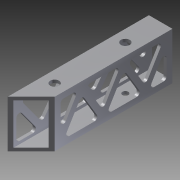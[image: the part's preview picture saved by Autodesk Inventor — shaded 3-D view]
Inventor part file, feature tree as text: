
AUTODESK INVENTOR PART (.ipt)
format: ipt  version: 2012 (Build 160160000, 160)  size: 280,064 bytes
history: native  units: in
note: dims shown in document units (in); Inventor stores cm internally (conversion verified against a paired STEP export)
features: extrude x6, sketch x5, fillet x1
ambient origin geometry x8: Origin, YZ Plane, XZ Plane, XY Plane, X Axis, Y Axis, Z Axis, Center Point
bodies: Solid1 (feature_tree)
feature tree (12):
  extrude  "Extrusion1"  Depth=1.0in
  sketch  "Sketch2"  dims[d2=0.125in d3=0.125in]
  extrude  "Extrusion2"  Depth=0.125in
  extrude  "Extrusion3"  Depth=0.125in
  extrude  "Extrusion4"  TaperAngle=45.0deg  [1 undecoded]
  extrude  "Extrusion5"  Depth=0.5in
  extrude  "Extrusion6"  Depth=1.5in
  fillet  "Fillet1"  Radius=3.0in
  sketch  "Sketch1"  dims[d0=2.0in d1=1.0in]
  sketch  "Sketch3"  dims[d4=0.125in d5=0.125in]
  sketch  "Sketch4"  dims[d6=6.0in d7=0.0in d8=45.0deg]
  sketch  "Sketch5"  dims[d9=0.25in d10=0.5in d11=1.5in d12=3.0in d13=0.125in d14=0.0in d15=0.125in d16=0.0in d17=0.375in d18=0.125in d19=0.0in d20=0.2128in d21=0.4255in d22=0.4255in d23=0.4255in d24=0.4255in d25=0.125in d26=0.125in d27=0.125in d28=0.125in d29=0.125in d30=0.125in d31=0.125in d32=0.125in d33=0.125in d34=0.125in d35=0.25in d36=0.25in d37=0.25in d38=0.25in d39=0.125in d40=0.0in d41=0.2491in d42=0.4982in d43=0.4982in d44=0.4982in d45=0.4982in d46=0.125in d47=0.125in d48=0.125in d49=0.125in d50=0.125in d51=0.125in d52=0.125in d53=0.125in d54=0.125in d55=0.125in d56=0.25in d57=0.25in d58=0.25in d59=0.25in d60=0.125in d61=0.0in d62=0.125in]
note: 1 required parameter value undecoded (feature->parameter linkage not recoverable at this tier; creation-order binding heuristic only, values carry confidence <= 0.55)
